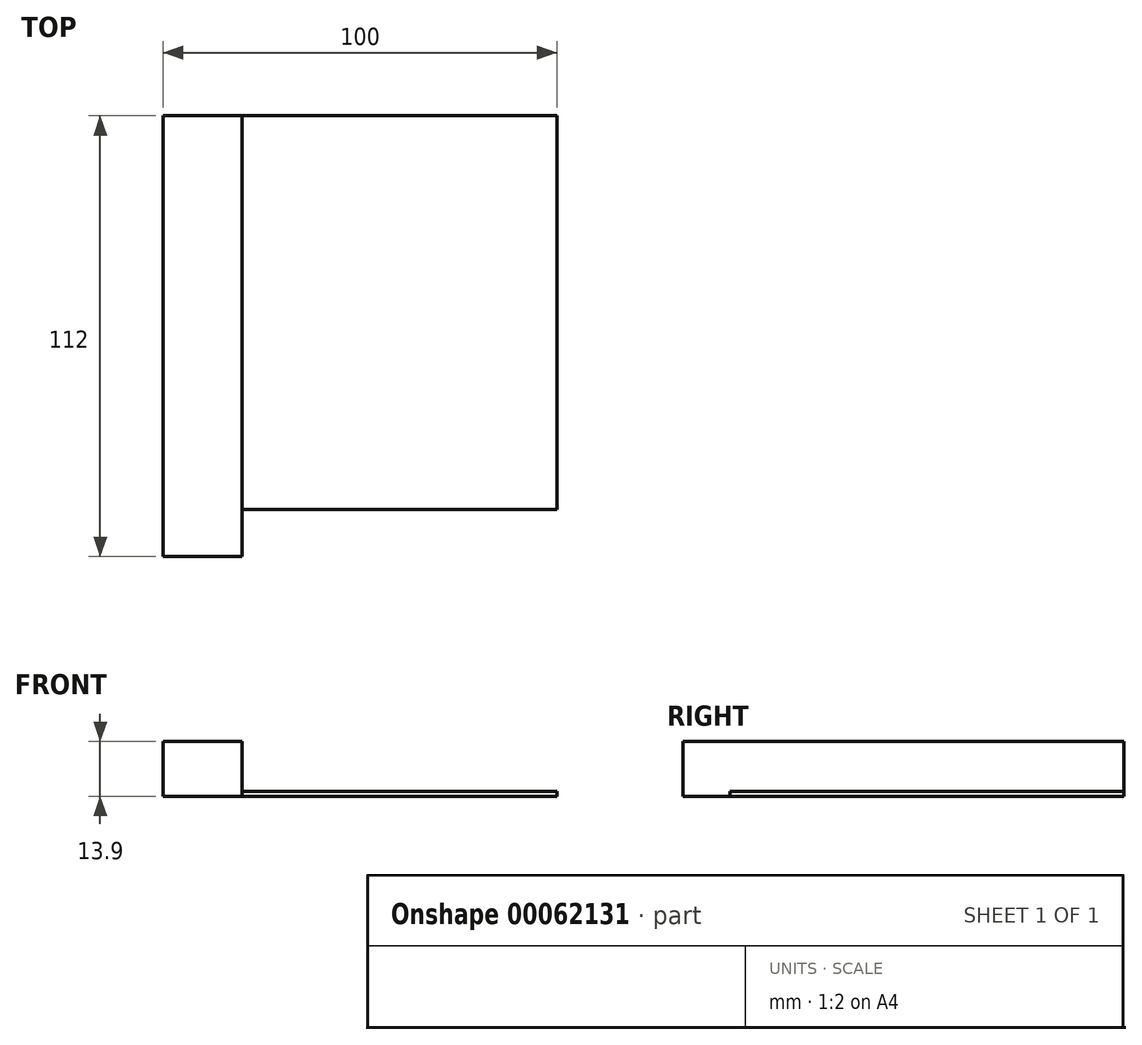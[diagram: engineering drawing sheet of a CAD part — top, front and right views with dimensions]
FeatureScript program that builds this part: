
annotation { "Feature Type Name" : "Feature", "Feature Type Description" : "" }
export const myFeature = defineFeature(function(context is Context, id is Id, definition is map)
    precondition{}
    {
        {
            var Q0;
            Q0=qCreatedBy(makeId("Top.planeOp"),FACE);
            var sketch = newSketch(context, id + "F0", { "sketchPlane" : qUnion([Q0])});
            skLineSegment(sketch, "E0.rect.bottom", {"start": v(50, 50) * mm, "end": v(-50, 50) * mm});
            skLineSegment(sketch, "E0.rect.top", {"start": v(50, -50) * mm, "end": v(-50, -50) * mm});
            skLineSegment(sketch, "E0.rect.left", {"start": v(50, 50) * mm, "end": v(50, -50) * mm});
            skLineSegment(sketch, "E0.rect.right", {"start": v(-50, 50) * mm, "end": v(-50, -50) * mm});
            skPoint(sketch, "E0.rect.middle", {"position": v(0, 0) * mm});
            skSolve(sketch);
        }
        {
            var Q0;
            Q0=makeQuery(id+"F0.imprint","IMPRINT",FACE,{"disambiguationData":[TD([[makeQuery(id+"F0.imprint","IMPRINT",EDGE,{"derivedFrom":sQuery(id+"F0.wireOp",EDGE,"E0.rect.bottom")}),1.0]])]});
            extrude(context, id + "F1", {"entities" : qUnion([Q0]), "depth" : 1.2 * mm});
        }
        {
            var Q0;
            Q0=makeQuery(id+"F1.opExtrude","CAP_FACE",FACE,{"disambiguationData":[OSD([sQuery(id+"F0.wireOp",EDGE,"E0.rect.bottom"),sQuery(id+"F0.wireOp",EDGE,"E0.rect.top"),sQuery(id+"F0.wireOp",EDGE,"E0.rect.left"),sQuery(id+"F0.wireOp",EDGE,"E0.rect.right")])],"isStart":false});
            var sketch = newSketch(context, id + "F2", { "sketchPlane" : qUnion([Q0])});
            skLineSegment(sketch, "E1.bottom", {"start": v(-50, 50) * mm, "end": v(-30, 50) * mm});
            skLineSegment(sketch, "E1.top", {"start": v(-50, -50) * mm, "end": v(-30, -50) * mm});
            skLineSegment(sketch, "E1.left", {"start": v(-50, 50) * mm, "end": v(-50, -50) * mm});
            skLineSegment(sketch, "E1.right", {"start": v(-30, 50) * mm, "end": v(-30, -50) * mm});
            skSolve(sketch);
        }
        {
            var Q0;
            Q0=makeQuery(id+"F2.imprint","IMPRINT",FACE,{"disambiguationData":[TD([[makeQuery(id+"F2.imprint","IMPRINT",EDGE,{"derivedFrom":sQuery(id+"F2.wireOp",EDGE,"E1.bottom")}),1.0]])]});
            extrude(context, id + "F3", {"entities" : qUnion([Q0]), "operationType" : NewBodyOperationType.ADD, "depth" : 12.7 * mm});
        }
        {
            var Q0;
            Q0=makeQuery(id+"F3.boolean.opBoolean","MERGE",FACE,{"derivedFrom":[makeQuery(id+"F1.opExtrude","SWEPT_FACE",FACE,{"disambiguationData":[OSD([sQuery(id+"F0.wireOp",EDGE,"E0.rect.top")])]}),makeQuery(id+"F3.opExtrude","SWEPT_FACE",FACE,{"disambiguationData":[OSD([sQuery(id+"F2.wireOp",EDGE,"E1.top")])]})]});
            var sketch = newSketch(context, id + "F4", { "sketchPlane" : qUnion([Q0])});
            skLineSegment(sketch, "E2.bottom", {"start": v(-50, 13.9) * mm, "end": v(-30, 13.9) * mm});
            skLineSegment(sketch, "E2.top", {"start": v(-50, 0) * mm, "end": v(-30, 0) * mm});
            skLineSegment(sketch, "E2.left", {"start": v(-50, 13.9) * mm, "end": v(-50, 0) * mm});
            skLineSegment(sketch, "E2.right", {"start": v(-30, 13.9) * mm, "end": v(-30, 0) * mm});
            skSolve(sketch);
        }
        {
            var Q0;
            {var subQ1=sQuery(id+"F4.wireOp",EDGE,"E2.bottom");Q0=makeQuery(id+"F4.imprint","IMPRINT",FACE,{"disambiguationData":[TD([[makeQuery(id+"F4.imprint","IMPRINT",EDGE,{"derivedFrom":subQ1}),1.0]])]});}
            extrude(context, id + "F5", {"entities" : qUnion([Q0]), "operationType" : NewBodyOperationType.ADD, "depth" : 12 * mm});
        }
    });
